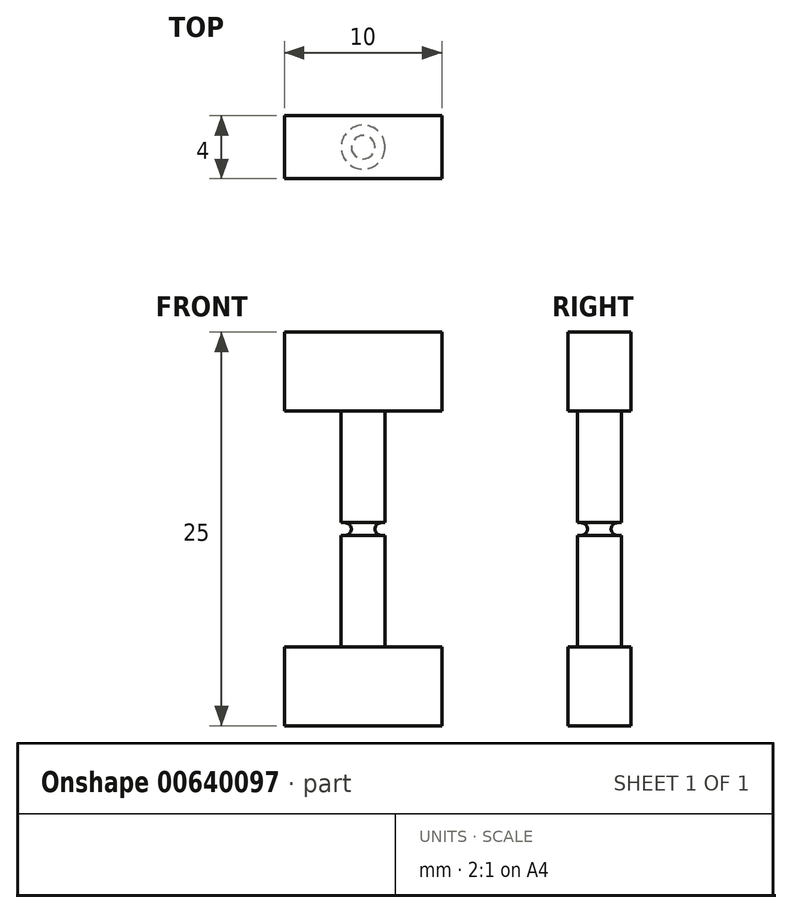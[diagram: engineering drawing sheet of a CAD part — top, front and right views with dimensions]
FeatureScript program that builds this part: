
annotation { "Feature Type Name" : "Feature", "Feature Type Description" : "" }
export const myFeature = defineFeature(function(context is Context, id is Id, definition is map)
    precondition{}
    {
        {
            var Q0;
            Q0=qCreatedBy(makeId("Front.planeOp"),FACE);
            var sketch = newSketch(context, id + "F0", { "sketchPlane" : qUnion([Q0])});
            skLineSegment(sketch, "E0.top", {"start": v(0, 7.5) * mm, "end": v(1.4, 7.5) * mm});
            skLineSegment(sketch, "E0.left", {"start": v(0, 0) * mm, "end": v(0, 7.5) * mm});
            skLineSegment(sketch, "E0.right", {"start": v(1.4, 0.4) * mm, "end": v(1.4, 7.5) * mm});
            skArc(sketch, "E1", {"start": v(1.15, 0.4) * mm, "mid": v(0.87, 0.28) * mm, "end": v(0.75, 0) * mm});
            skLineSegment(sketch, "E2", {"start": v(1.15, 0.4) * mm, "end": v(1.4, 0.4) * mm});
            skLineSegment(sketch, "E3.MirrorCS", {"start": v(0, -7.5) * mm, "end": v(1.4, -7.5) * mm});
            skLineSegment(sketch, "E4.MirrorCS", {"start": v(1.15, -0.4) * mm, "end": v(1.4, -0.4) * mm});
            skArc(sketch, "E5.MirrorCS", {"start": v(1.15, -0.4) * mm, "mid": v(0.87, -0.28) * mm, "end": v(0.75, 0) * mm});
            skLineSegment(sketch, "E6.MirrorCS", {"start": v(1.4, -0.4) * mm, "end": v(1.4, -7.5) * mm});
            skLineSegment(sketch, "E7.MirrorCS", {"start": v(0, 0) * mm, "end": v(0, -7.5) * mm});
            skSolve(sketch);
        }
        {
            var Q0;
            Q0 = qSketchRegion(id + "F0", true);
            var Q1;
            Q1=sQuery(id+"F0.wireOp",EDGE,"E0.left");
            revolve(context, id + "F1", {"entities" : qUnion([Q0]), "axis" : qUnion([Q1]), "revolveType" : RevolveType.FULL});
        }
        {
            var Q0;
            Q0=makeQuery(id+"F1.opRevolve","SWEPT_FACE",FACE,{"disambiguationData":[OSD([sQuery(id+"F0.wireOp",EDGE,"E0.top")])]});
            var sketch = newSketch(context, id + "F2", { "sketchPlane" : qUnion([Q0])});
            skLineSegment(sketch, "E8.bottom", {"start": v(-5, -2) * mm, "end": v(5, -2) * mm});
            skLineSegment(sketch, "E8.top", {"start": v(-5, 2) * mm, "end": v(5, 2) * mm});
            skLineSegment(sketch, "E8.left", {"start": v(-5, -2) * mm, "end": v(-5, 2) * mm});
            skLineSegment(sketch, "E8.right", {"start": v(5, -2) * mm, "end": v(5, 2) * mm});
            skPoint(sketch, "E8.middle", {"position": v(0, 0) * mm});
            skSolve(sketch);
        }
        {
            var Q0;
            Q0=makeQuery(id+"F2.imprint","IMPRINT",FACE,{"disambiguationData":[TD([[makeQuery(id+"F2.imprint","IMPRINT",EDGE,{"derivedFrom":makeQuery(id+"F1.opRevolve","SWEPT_EDGE",EDGE,{"disambiguationData":[OSD([sQuery(id+"F0.wireOp",EDGE,"E0.top"),sQuery(id+"F0.wireOp",EDGE,"E0.right")])]})}),-1.0]])]});
            var Q1;
            Q1=makeQuery(id+"F2.imprint","IMPRINT",FACE,{"disambiguationData":[TD([[makeQuery(id+"F2.imprint","IMPRINT",EDGE,{"derivedFrom":sQuery(id+"F2.wireOp",EDGE,"E8.bottom")}),1.0]])]});
            extrude(context, id + "F3", {"entities" : qUnion([Q0, Q1]), "operationType" : NewBodyOperationType.ADD, "depth" : 5 * mm, "offsetDistance" : 25 * mm});
        }
        {
            var Q0;
            Q0=makeQuery(id+"F1.opRevolve","SWEPT_FACE",FACE,{"disambiguationData":[OSD([sQuery(id+"F0.wireOp",EDGE,"E3.MirrorCS")])]});
            var sketch = newSketch(context, id + "F4", { "sketchPlane" : qUnion([Q0])});
            skLineSegment(sketch, "E9.bottom", {"start": v(5, 2) * mm, "end": v(-5, 2) * mm});
            skLineSegment(sketch, "E9.top", {"start": v(5, -2) * mm, "end": v(-5, -2) * mm});
            skLineSegment(sketch, "E9.left", {"start": v(5, 2) * mm, "end": v(5, -2) * mm});
            skLineSegment(sketch, "E9.right", {"start": v(-5, 2) * mm, "end": v(-5, -2) * mm});
            skPoint(sketch, "E9.middle", {"position": v(0, 0) * mm});
            skSolve(sketch);
        }
        {
            var Q0;
            Q0=makeQuery(id+"F4.imprint","IMPRINT",FACE,{"disambiguationData":[TD([[makeQuery(id+"F4.imprint","IMPRINT",EDGE,{"derivedFrom":makeQuery(id+"F1.opRevolve","SWEPT_EDGE",EDGE,{"disambiguationData":[OSD([sQuery(id+"F0.wireOp",EDGE,"E3.MirrorCS"),sQuery(id+"F0.wireOp",EDGE,"E6.MirrorCS")])]})}),1.0]])]});
            var Q1;
            Q1=makeQuery(id+"F4.imprint","IMPRINT",FACE,{"disambiguationData":[TD([[makeQuery(id+"F4.imprint","IMPRINT",EDGE,{"derivedFrom":sQuery(id+"F4.wireOp",EDGE,"E9.bottom")}),1.0]])]});
            extrude(context, id + "F5", {"entities" : qUnion([Q0, Q1]), "operationType" : NewBodyOperationType.ADD, "depth" : 5 * mm, "offsetDistance" : 25 * mm});
        }
    });
